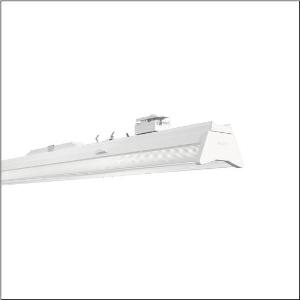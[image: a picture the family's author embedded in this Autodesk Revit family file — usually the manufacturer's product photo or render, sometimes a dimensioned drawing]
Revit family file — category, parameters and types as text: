
# Revit family: licross_11_performance_mo_51td16cn49xg
name_source: partatom
category: Lighting Fixtures
units: mm (PartAtom-declared; Revit-internal decimal feet)

## family parameters
Cut with Voids When Loaded = No
Host = Face
Light Source = No
Part Type = Normal
Room Calculation Point = No
Round Connector Dimension = Use Diameter
Shared = No

## types (1)
- --- (1 x LED, 9190 lm, 49.4 W, 4000K)
    Apparent Load = 49 VA
    CIE Flux Codes = 66 88 96 79 100
    Color Rendering = 80
    Color Temperature = 4000K
    Default Elevation = 1800 mm
    Description = Licross 11 Performance MO, luminaire insert, of sheet steel, galvanised, coil coated, white, length: 1.500mm, width: 120mm, height: 123mm, LED rated luminous flux: 9.190lm, light colour: 840, SDCM (Standard Deviation of Colour Matching)MacAdam ≤ 2 SDCM (initial), control gear: ON/OFF Multilumen, CLOi, with plug, 3-pole, with phase selection, mains connection: 220..240V, AC, 50/60Hz, start of lifetime: 49W, end of service life: 55W, internal wiring halogen-free, primary light control with lens, of plastic, primary optical cover: cover, of PMMA, light emission: direct/indirect distribution, primary light characteristic: symmetric, protection rating (complete): IP54, insulation class (complete): insulation class I (protective earthing), certification: CE, ENEC, VDE, UKCA, protection symbol: D if used in an environment with non-conductive dust loads with corresponding accessories, impact resistance: IK06, permissible ambient temperature for indoor applications: -35..+40°C, corresponds to IFS (International Featured Standards) requirements for safety and quality in the food industry, reducing of maximum allowable ambient temperature of 5°C with ceiling mounting, LABS conformity tested according to VDMA 24364:2018-05, The light source and the operating device comply with the requirements of the Ecodesign Regulation (EU) 2019/2020 and are replaceable in accordance with this regulation, packaging unit: 1 piece
    Height = 114 mm
    Lamp = 1 x LED
    Lamp Light Flux = 9190 lm
    Lamp Power = 49.4 W
    Lamp count = 1
    Length = 1500 mm
    Luminous efficacy = 186 lm/W
    Manufacturer = Siteco
    ModVariant = No
    Model = 51TD16CN49XG
    Mounting Place = Ceiling
    Mounting Type = Pendant
    Number of Poles = 1
    OnlyDefault = Yes
    Power Factor = 1
    Product Name = Licross 11 Performance MO
    Product group = luminaire insert | ceiling pendant
    ProductGroupID = 901
    Protection Class = Protection class I
    Protection Degree = IP 54
    RLX_Detail_Level = 1
    RLX_Emergency_Light_Flux = 0 lm
    RLX_Emergency_Type = 0
    RLX_Emergency_Type_DB = No
    RlxData = <blob elided: 32113 chars, md5=b9f652f5>
    Socket = socket
    Standby Power = 0 W
    System Light Flux = 9190 lm
    System Power = 49 W
    Type Comments = factory setting: luminous flux: 100 % | (A | C | E) | 113 mA
    Type Image = l_1256138.jpg
    URL = http://relux.com
    VarID = @adj_001015
    Voltage = 0 V
    Weight = 0.00 kg
    Width = 120 mm

## geometry (parser evidence)
native form markers: Blend x4, Sweep x12
no freeform markers — native parametric forms only
